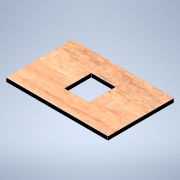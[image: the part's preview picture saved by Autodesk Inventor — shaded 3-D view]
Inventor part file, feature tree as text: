
AUTODESK INVENTOR PART (.ipt)
format: ipt  version: 2021 (Build 250183000, 183)  size: 121,344 bytes
history: native  units: mm
features: extrude x1, sketch x1
ambient origin geometry x8: Origin, YZ Plane, XZ Plane, XY Plane, X Axis, Y Axis, Z Axis, Center Point
bodies: Volumenkörper1 (feature_tree)
feature tree (2):
  extrude  "Extrusion1"  Depth=51.5mm
  sketch  "Skizze1"  dims[d0=79.5mm d1=51.5mm d2=3.0mm d3=0.0mm d4=21.0mm d5=19.0mm]
